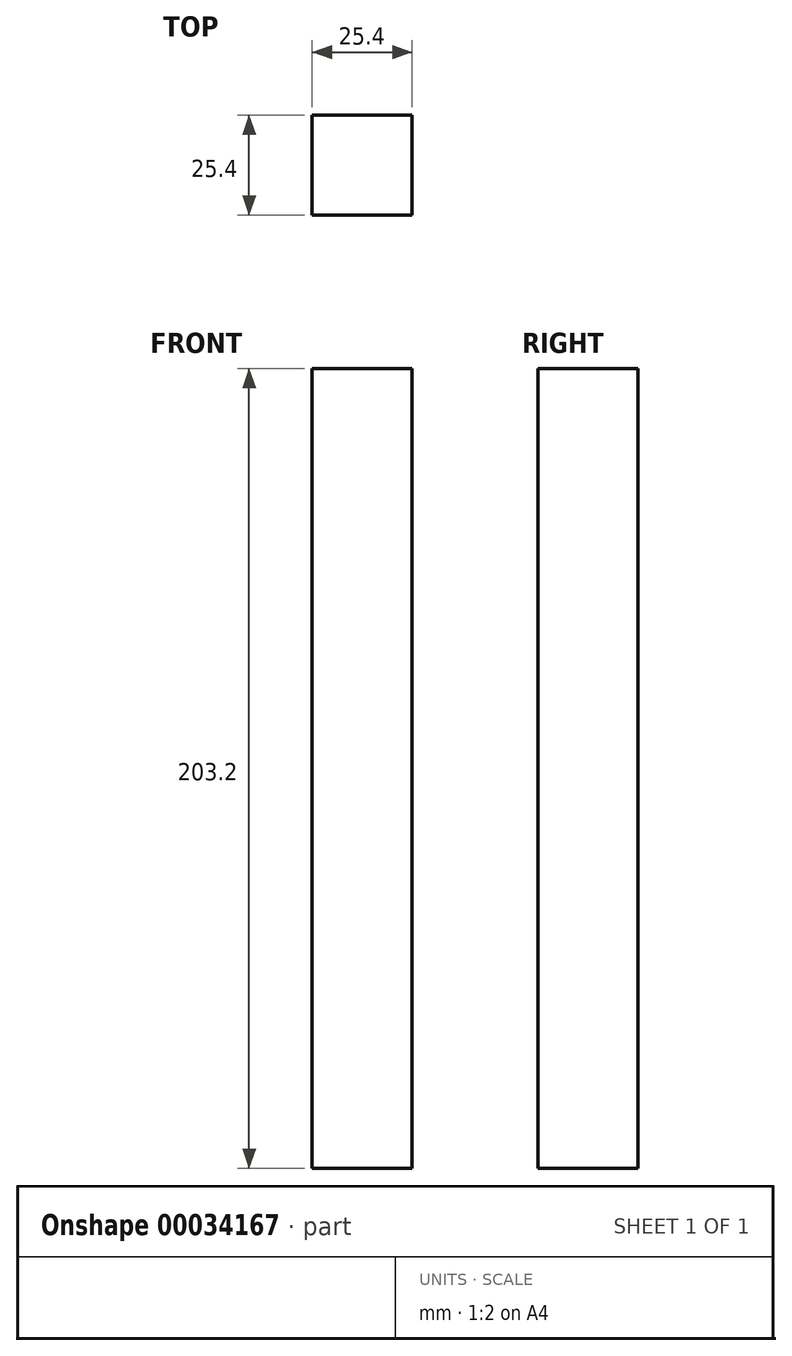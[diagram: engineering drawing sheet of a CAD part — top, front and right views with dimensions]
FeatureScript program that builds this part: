
annotation { "Feature Type Name" : "Feature", "Feature Type Description" : "" }
export const myFeature = defineFeature(function(context is Context, id is Id, definition is map)
    precondition{}
    {
        {
            var Q0;
            Q0=qCreatedBy(makeId("Top.planeOp"),FACE);
            var sketch = newSketch(context, id + "F0", { "sketchPlane" : qUnion([Q0])});
            skLineSegment(sketch, "E0.rect.bottom", {"start": v(12.7, 12.7) * mm, "end": v(-12.7, 12.7) * mm});
            skLineSegment(sketch, "E0.rect.top", {"start": v(12.7, -12.7) * mm, "end": v(-12.7, -12.7) * mm});
            skLineSegment(sketch, "E0.rect.left", {"start": v(12.7, 12.7) * mm, "end": v(12.7, -12.7) * mm});
            skLineSegment(sketch, "E0.rect.right", {"start": v(-12.7, 12.7) * mm, "end": v(-12.7, -12.7) * mm});
            skPoint(sketch, "E0.rect.middle", {"position": v(0, 0) * mm});
            skSolve(sketch);
        }
        {
            var Q0;
            Q0 = qSketchRegion(id + "F0", true);
            extrude(context, id + "F1", {"entities" : qUnion([Q0]), "depth" : 203.2 * mm});
        }
    });
